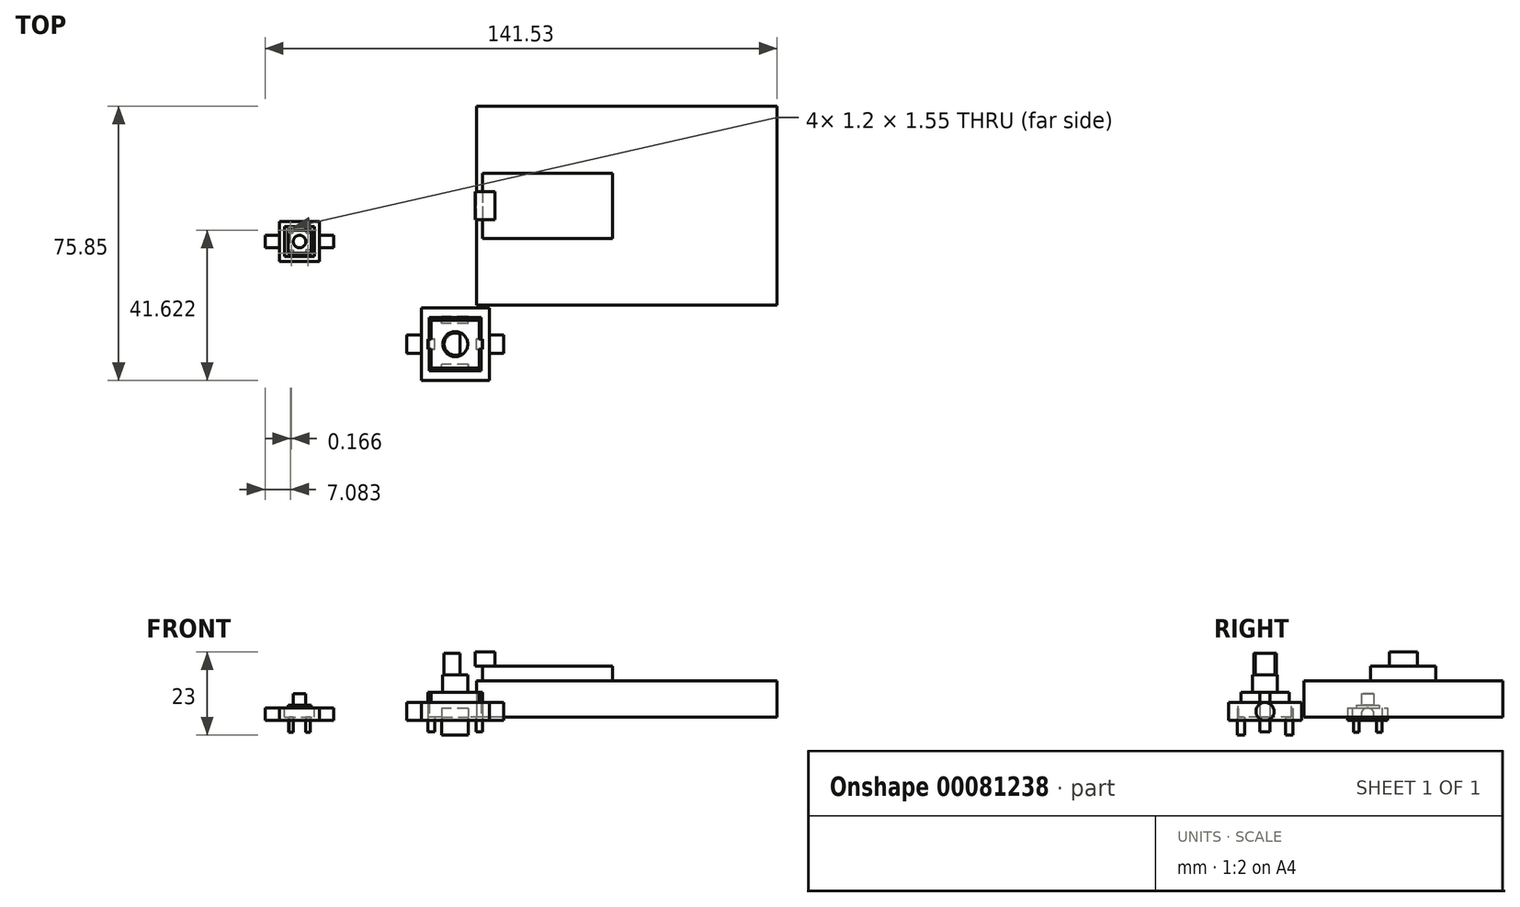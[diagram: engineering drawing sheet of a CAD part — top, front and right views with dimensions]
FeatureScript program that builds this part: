
annotation { "Feature Type Name" : "Feature", "Feature Type Description" : "" }
export const myFeature = defineFeature(function(context is Context, id is Id, definition is map)
    precondition{}
    {
        {
            var Q0;
            Q0=qCreatedBy(makeId("Top.planeOp"),FACE);
            var sketch = newSketch(context, id + "F0", { "sketchPlane" : qUnion([Q0])});
            skLineSegment(sketch, "E0.bottom", {"start": v(-39.86, 25.2) * mm, "end": v(-46.2, 25.2) * mm});
            skLineSegment(sketch, "E0.top", {"start": v(-39.86, 31.54) * mm, "end": v(-46.2, 31.54) * mm});
            skLineSegment(sketch, "E0.left", {"start": v(-39.86, 25.2) * mm, "end": v(-39.86, 31.54) * mm});
            skLineSegment(sketch, "E0.right", {"start": v(-46.2, 25.2) * mm, "end": v(-46.2, 31.54) * mm});
            skPoint(sketch, "E0.middle", {"position": v(-43.03, 28.37) * mm});
            skSolve(sketch);
        }
        {
            var Q0;
            Q0 = qSketchRegion(id + "F0", true);
            extrude(context, id + "F1", {"entities" : qUnion([Q0]), "depth" : 3.3 * mm});
        }
        {
            var Q0;
            Q0=makeQuery(id+"F1.opExtrude","SWEPT_FACE",FACE,{"disambiguationData":[OSD([sQuery(id+"F0.wireOp",EDGE,"E0.bottom")])]});
            var sketch = newSketch(context, id + "F2", { "sketchPlane" : qUnion([Q0])});
            skLineSegment(sketch, "E1.bottom", {"start": v(-40.12, 0.6) * mm, "end": v(-41.32, 0.6) * mm});
            skLineSegment(sketch, "E1.top", {"start": v(-40.12, -4.2) * mm, "end": v(-41.32, -4.2) * mm});
            skLineSegment(sketch, "E1.left", {"start": v(-40.12, 0.6) * mm, "end": v(-40.12, -4.2) * mm});
            skLineSegment(sketch, "E1.right", {"start": v(-41.32, 0.6) * mm, "end": v(-41.32, -4.2) * mm});
            skLineSegment(sketch, "E2", {"start": v(-43.03, 3.3) * mm, "end": v(-43.03, 2.27) * mm, "construction": true});
            skPoint(sketch, "E2.endSnap0", {"position": v(-43.03, 3.3) * mm});
            skLineSegment(sketch, "E3.MirrorCS", {"start": v(-44.74, 0.6) * mm, "end": v(-44.74, -4.2) * mm});
            skLineSegment(sketch, "E4.MirrorCS", {"start": v(-45.94, 0.6) * mm, "end": v(-44.74, 0.6) * mm});
            skLineSegment(sketch, "E5.MirrorCS", {"start": v(-45.94, 0.6) * mm, "end": v(-45.94, -4.2) * mm});
            skLineSegment(sketch, "E6.MirrorCS", {"start": v(-45.94, -4.2) * mm, "end": v(-44.74, -4.2) * mm});
            skSolve(sketch);
        }
        {
            var Q0;
            Q0=makeQuery(id+"F1.opExtrude","SWEPT_FACE",FACE,{"disambiguationData":[OSD([sQuery(id+"F0.wireOp",EDGE,"E0.top")])]});
            var sketch = newSketch(context, id + "F3", { "sketchPlane" : qUnion([Q0])});
            skLineSegment(sketch, "E7.bottom", {"start": v(46.1, 0.58) * mm, "end": v(44.9, 0.58) * mm});
            skLineSegment(sketch, "E7.top", {"start": v(46.1, -4.22) * mm, "end": v(44.9, -4.22) * mm});
            skLineSegment(sketch, "E7.left", {"start": v(46.1, 0.58) * mm, "end": v(46.1, -4.22) * mm});
            skLineSegment(sketch, "E7.right", {"start": v(44.9, 0.58) * mm, "end": v(44.9, -4.22) * mm});
            skLineSegment(sketch, "E8", {"start": v(43.09, 5.78) * mm, "end": v(43.09, 4.76) * mm, "construction": true});
            skPoint(sketch, "E8.endSnap0", {"position": v(43.09, 3.28) * mm});
            skLineSegment(sketch, "E9.MirrorCS", {"start": v(41.27, 0.58) * mm, "end": v(41.27, -4.22) * mm});
            skLineSegment(sketch, "E10.MirrorCS", {"start": v(40.07, 0.58) * mm, "end": v(41.27, 0.58) * mm});
            skLineSegment(sketch, "E11.MirrorCS", {"start": v(40.07, 0.58) * mm, "end": v(40.07, -4.22) * mm});
            skLineSegment(sketch, "E12.MirrorCS", {"start": v(40.07, -4.22) * mm, "end": v(41.27, -4.22) * mm});
            skSolve(sketch);
        }
        {
            var Q0;
            Q0 = qSketchRegion(id + "F3", true);
            var Q1;
            Q1 = qSketchRegion(id + "F2", true);
            extrude(context, id + "F4", {"entities" : qUnion([Q0, Q1]), "operationType" : NewBodyOperationType.ADD, "endBound" : BoundingType.SYMMETRIC, "depth" : 1.55 * mm});
        }
        {
            var Q0;
            Q0=makeQuery(id+"F1.opExtrude","CAP_FACE",FACE,{"disambiguationData":[OSD([sQuery(id+"F0.wireOp",EDGE,"E0.bottom"),sQuery(id+"F0.wireOp",EDGE,"E0.top"),sQuery(id+"F0.wireOp",EDGE,"E0.left"),sQuery(id+"F0.wireOp",EDGE,"E0.right")])],"isStart":false});
            var sketch = newSketch(context, id + "F5", { "sketchPlane" : qUnion([Q0])});
            skCircle(sketch, "E13", {"center": v(-43.03, 28.37) * mm, "radius": 1.73 * mm});
            skPoint(sketch, "E13.centerSnap0", {"position": v(-43.03, 31.54) * mm});
            skPoint(sketch, "E13.centerSnap1", {"position": v(-39.86, 28.37) * mm});
            skSolve(sketch);
        }
        {
            var Q0;
            Q0 = qSketchRegion(id + "F5", true);
            extrude(context, id + "F6", {"entities" : qUnion([Q0]), "operationType" : NewBodyOperationType.ADD, "depth" : 3.19 * mm});
        }
        {
            var Q0;
            Q0=qCreatedBy(makeId("Top.planeOp"),FACE);
            var sketch = newSketch(context, id + "F7", { "sketchPlane" : qUnion([Q0])});
            skLineSegment(sketch, "E14.bottom", {"start": v(-6.65, -6.65) * mm, "end": v(6.65, -6.65) * mm});
            skLineSegment(sketch, "E14.top", {"start": v(-6.65, 6.65) * mm, "end": v(6.65, 6.65) * mm});
            skLineSegment(sketch, "E14.left", {"start": v(-6.65, -6.65) * mm, "end": v(-6.65, 6.65) * mm});
            skLineSegment(sketch, "E14.right", {"start": v(6.65, -6.65) * mm, "end": v(6.65, 6.65) * mm});
            skPoint(sketch, "E14.middle", {"position": v(0, 0) * mm});
            skSolve(sketch);
        }
        {
            var Q0;
            Q0 = qSketchRegion(id + "F7", true);
            extrude(context, id + "F8", {"entities" : qUnion([Q0]), "depth" : 6.8 * mm});
        }
        {
            var Q0;
            Q0=makeQuery(id+"F8.opExtrude","SWEPT_FACE",FACE,{"disambiguationData":[OSD([sQuery(id+"F7.wireOp",EDGE,"E14.left")])]});
            var sketch = newSketch(context, id + "F9", { "sketchPlane" : qUnion([Q0])});
            skLineSegment(sketch, "E15.bottom", {"start": v(-1.36, 6.8) * mm, "end": v(1.44, 6.8) * mm});
            skLineSegment(sketch, "E15.top", {"start": v(-1.36, -4.1) * mm, "end": v(1.44, -4.1) * mm});
            skLineSegment(sketch, "E15.left", {"start": v(-1.36, 6.8) * mm, "end": v(-1.36, -4.1) * mm});
            skLineSegment(sketch, "E15.right", {"start": v(1.44, 6.8) * mm, "end": v(1.44, -4.1) * mm});
            skSolve(sketch);
        }
        {
            var Q0;
            Q0=makeQuery(id+"F8.opExtrude","SWEPT_FACE",FACE,{"disambiguationData":[OSD([sQuery(id+"F7.wireOp",EDGE,"E14.right")])]});
            var sketch = newSketch(context, id + "F10", { "sketchPlane" : qUnion([Q0])});
            skLineSegment(sketch, "E16.bottom", {"start": v(-1.46, 6.8) * mm, "end": v(1.34, 6.8) * mm});
            skLineSegment(sketch, "E16.top", {"start": v(-1.46, -4.1) * mm, "end": v(1.34, -4.1) * mm});
            skLineSegment(sketch, "E16.left", {"start": v(-1.46, 6.8) * mm, "end": v(-1.46, -4.1) * mm});
            skLineSegment(sketch, "E16.right", {"start": v(1.34, 6.8) * mm, "end": v(1.34, -4.1) * mm});
            skSolve(sketch);
        }
        {
            var Q0;
            Q0 = qSketchRegion(id + "F10", true);
            var Q1;
            Q1 = qSketchRegion(id + "F9", true);
            extrude(context, id + "F11", {"entities" : qUnion([Q0, Q1]), "operationType" : NewBodyOperationType.ADD, "endBound" : BoundingType.SYMMETRIC, "depth" : 1.85 * mm});
        }
        {
            var Q0;
            Q0=makeQuery(id+"F8.opExtrude","SWEPT_FACE",FACE,{"disambiguationData":[OSD([sQuery(id+"F7.wireOp",EDGE,"E14.top")])]});
            var sketch = newSketch(context, id + "F12", { "sketchPlane" : qUnion([Q0])});
            skLineSegment(sketch, "E17.bottom", {"start": v(-3.55, 2.3) * mm, "end": v(3.75, 2.3) * mm});
            skLineSegment(sketch, "E17.top", {"start": v(-3.55, -5) * mm, "end": v(3.75, -5) * mm});
            skLineSegment(sketch, "E17.left", {"start": v(-3.55, 2.3) * mm, "end": v(-3.55, -5) * mm});
            skLineSegment(sketch, "E17.right", {"start": v(3.75, 2.3) * mm, "end": v(3.75, -5) * mm});
            skSolve(sketch);
        }
        {
            var Q0;
            Q0=makeQuery(id+"F8.opExtrude","SWEPT_FACE",FACE,{"disambiguationData":[OSD([sQuery(id+"F7.wireOp",EDGE,"E14.bottom")])]});
            var sketch = newSketch(context, id + "F13", { "sketchPlane" : qUnion([Q0])});
            skLineSegment(sketch, "E18.0", {"start": v(3.55, 2.3) * mm, "end": v(-3.75, 2.3) * mm});
            skLineSegment(sketch, "E19.0", {"start": v(-3.75, 2.3) * mm, "end": v(-3.75, -5) * mm});
            skLineSegment(sketch, "E20.0", {"start": v(3.55, -5) * mm, "end": v(-3.75, -5) * mm});
            skLineSegment(sketch, "E21.0", {"start": v(3.55, 2.3) * mm, "end": v(3.55, -5) * mm});
            skSolve(sketch);
        }
        {
            var Q0;
            Q0 = qSketchRegion(id + "F13", true);
            var Q1;
            Q1 = qSketchRegion(id + "F12", true);
            extrude(context, id + "F14", {"entities" : qUnion([Q0, Q1]), "operationType" : NewBodyOperationType.ADD, "endBound" : BoundingType.SYMMETRIC, "depth" : 2 * mm});
        }
        {
            var Q0;
            Q0=makeQuery(id+"F11.boolean.opBoolean","MERGE",FACE,{"derivedFrom":[makeQuery(id+"F8.opExtrude","CAP_FACE",FACE,{"disambiguationData":[OSD([sQuery(id+"F7.wireOp",EDGE,"E14.bottom"),sQuery(id+"F7.wireOp",EDGE,"E14.top"),sQuery(id+"F7.wireOp",EDGE,"E14.left"),sQuery(id+"F7.wireOp",EDGE,"E14.right")])],"isStart":false}),makeQuery(id+"F11.opExtrude","SWEPT_FACE",FACE,{"disambiguationData":[OSD([sQuery(id+"F9.wireOp",EDGE,"E15.bottom")])]}),makeQuery(id+"F11.opExtrude","SWEPT_FACE",FACE,{"disambiguationData":[OSD([sQuery(id+"F10.wireOp",EDGE,"E16.bottom")])]})]});
            var sketch = newSketch(context, id + "F15", { "sketchPlane" : qUnion([Q0])});
            skCircle(sketch, "E22", {"center": v(0, 0) * mm, "radius": 3.45 * mm});
            skSolve(sketch);
        }
        {
            var Q0;
            Q0 = qSketchRegion(id + "F15", true);
            extrude(context, id + "F16", {"entities" : qUnion([Q0]), "operationType" : NewBodyOperationType.ADD, "depth" : 4.8 * mm});
        }
        {
            var Q0;
            Q0=makeQuery(id+"F16.opExtrude","CAP_FACE",FACE,{"disambiguationData":[OSD([sQuery(id+"F15.wireOp",EDGE,"E22")])],"isStart":false});
            var sketch = newSketch(context, id + "F17", { "sketchPlane" : qUnion([Q0])});
            skCircle(sketch, "E23", {"center": v(0, 0) * mm, "radius": 3.08 * mm});
            skSolve(sketch);
        }
        {
            var Q0;
            Q0 = qSketchRegion(id + "F17", true);
            extrude(context, id + "F18", {"entities" : qUnion([Q0]), "operationType" : NewBodyOperationType.ADD, "depth" : 6 * mm});
        }
        {
            var Q0;
            Q0=makeQuery(id+"F18.opExtrude","CAP_FACE",FACE,{"disambiguationData":[OSD([sQuery(id+"F17.wireOp",EDGE,"E23")])],"isStart":false});
            var sketch = newSketch(context, id + "F19", { "sketchPlane" : qUnion([Q0])});
            skArc(sketch, "E24.0", {"start": v(1.38, -2.75) * mm, "mid": v(3.08, 0) * mm, "end": v(1.38, 2.75) * mm});
            skLineSegment(sketch, "E25", {"start": v(1.38, 2.75) * mm, "end": v(1.38, -2.75) * mm});
            skLineSegment(sketch, "E26", {"start": v(1.82, 0) * mm, "end": v(3.08, 0) * mm, "construction": true});
            skSolve(sketch);
        }
        {
            var Q0;
            Q0 = qSketchRegion(id + "F19", true);
            var Q1;
            Q1=makeQuery(id+"F16.opExtrude","CAP_FACE",FACE,{"disambiguationData":[OSD([sQuery(id+"F15.wireOp",EDGE,"E22")])],"isStart":false});
            extrude(context, id + "F20", {"entities" : qUnion([Q0]), "operationType" : NewBodyOperationType.REMOVE, "endBound" : BoundingType.UP_TO_SURFACE, "oppositeDirection" : true, "endBoundEntityFace" : qUnion([Q1]), "depth" : 25 * mm});
        }
        {
            var Q0;
            Q0=qCreatedBy(makeId("Top.planeOp"),FACE);
            var sketch = newSketch(context, id + "F21", { "sketchPlane" : qUnion([Q0])});
            skLineSegment(sketch, "E27.bottom", {"start": v(88.94, 10.77) * mm, "end": v(5.94, 10.77) * mm});
            skLineSegment(sketch, "E27.top", {"start": v(88.94, 65.77) * mm, "end": v(5.94, 65.77) * mm});
            skLineSegment(sketch, "E27.left", {"start": v(88.94, 10.77) * mm, "end": v(88.94, 65.77) * mm});
            skLineSegment(sketch, "E27.right", {"start": v(5.94, 10.77) * mm, "end": v(5.94, 65.77) * mm});
            skPoint(sketch, "E27.middle", {"position": v(47.44, 38.27) * mm});
            skSolve(sketch);
        }
        {
            var Q0;
            Q0 = qSketchRegion(id + "F21", true);
            extrude(context, id + "F22", {"entities" : qUnion([Q0]), "depth" : 10 * mm});
        }
        {
            var Q0;
            Q0=makeQuery(id+"F22.opExtrude","CAP_FACE",FACE,{"disambiguationData":[OSD([sQuery(id+"F21.wireOp",EDGE,"E27.bottom"),sQuery(id+"F21.wireOp",EDGE,"E27.top"),sQuery(id+"F21.wireOp",EDGE,"E27.left"),sQuery(id+"F21.wireOp",EDGE,"E27.right")])],"isStart":false});
            var sketch = newSketch(context, id + "F23", { "sketchPlane" : qUnion([Q0])});
            skLineSegment(sketch, "E28.bottom", {"start": v(7.53, 47.27) * mm, "end": v(43.53, 47.27) * mm});
            skLineSegment(sketch, "E28.top", {"start": v(7.53, 29.17) * mm, "end": v(43.53, 29.17) * mm});
            skLineSegment(sketch, "E28.left", {"start": v(7.53, 47.27) * mm, "end": v(7.53, 29.17) * mm});
            skLineSegment(sketch, "E28.right", {"start": v(43.53, 47.27) * mm, "end": v(43.53, 29.17) * mm});
            skSolve(sketch);
        }
        {
            var Q0;
            Q0 = qSketchRegion(id + "F23", true);
            extrude(context, id + "F24", {"entities" : qUnion([Q0]), "operationType" : NewBodyOperationType.ADD, "depth" : 4 * mm});
        }
        {
            var Q0;
            Q0=makeQuery(id+"F24.opExtrude","CAP_FACE",FACE,{"disambiguationData":[OSD([sQuery(id+"F23.wireOp",EDGE,"E28.bottom"),sQuery(id+"F23.wireOp",EDGE,"E28.top"),sQuery(id+"F23.wireOp",EDGE,"E28.left"),sQuery(id+"F23.wireOp",EDGE,"E28.right")])],"isStart":false});
            var sketch = newSketch(context, id + "F25", { "sketchPlane" : qUnion([Q0])});
            skLineSegment(sketch, "E29.bottom", {"start": v(11.03, 42.12) * mm, "end": v(5.53, 42.12) * mm});
            skLineSegment(sketch, "E29.top", {"start": v(11.03, 34.42) * mm, "end": v(5.53, 34.42) * mm});
            skLineSegment(sketch, "E29.left", {"start": v(11.03, 42.12) * mm, "end": v(11.03, 34.42) * mm});
            skLineSegment(sketch, "E29.right", {"start": v(5.53, 42.12) * mm, "end": v(5.53, 34.42) * mm});
            skSolve(sketch);
        }
        {
            var Q0;
            Q0 = qSketchRegion(id + "F25", true);
            extrude(context, id + "F26", {"entities" : qUnion([Q0]), "operationType" : NewBodyOperationType.ADD, "depth" : 4 * mm});
        }
        {
            var Q0;
            Q0=makeQuery(id+"F1.opExtrude","CAP_FACE",FACE,{"disambiguationData":[OSD([sQuery(id+"F0.wireOp",EDGE,"E0.bottom"),sQuery(id+"F0.wireOp",EDGE,"E0.top"),sQuery(id+"F0.wireOp",EDGE,"E0.left"),sQuery(id+"F0.wireOp",EDGE,"E0.right")])],"isStart":true});
            var sketch = newSketch(context, id + "F27", { "sketchPlane" : qUnion([Q0])});
            skLineSegment(sketch, "E30.bottom", {"start": v(-37.59, -22.87) * mm, "end": v(-48.59, -22.87) * mm});
            skLineSegment(sketch, "E30.top", {"start": v(-37.59, -33.87) * mm, "end": v(-48.59, -33.87) * mm});
            skLineSegment(sketch, "E30.left", {"start": v(-37.59, -22.87) * mm, "end": v(-37.59, -33.87) * mm});
            skLineSegment(sketch, "E30.right", {"start": v(-48.59, -22.87) * mm, "end": v(-48.59, -33.87) * mm});
            skPoint(sketch, "E30.middle", {"position": v(-43.09, -28.37) * mm});
            skPoint(sketch, "E30.middle.positionSnap0", {"position": v(-43.09, -31.54) * mm});
            skPoint(sketch, "E30.middle.positionSnap1", {"position": v(-46.2, -28.37) * mm});
            skPoint(sketch, "E30.centerSnap0", {"position": v(-43.09, -31.54) * mm});
            skPoint(sketch, "E30.centerSnap1", {"position": v(-46.2, -28.37) * mm});
            skSolve(sketch);
        }
        {
            var Q0;
            Q0 = qSketchRegion(id + "F27", true);
            extrude(context, id + "F28", {"entities" : qUnion([Q0]), "oppositeDirection" : true, "depth" : 2.5 * mm, "hasSecondDirection" : true, "secondDirectionOppositeDirection" : false, "secondDirectionDepth" : 1 * mm});
        }
        {
            var Q0;
            Q0=makeQuery(id+"F1.opExtrude","SWEPT_BODY",BODY,{"disambiguationData":[OSD([sQuery(id+"F0.wireOp",EDGE,"E0.bottom"),sQuery(id+"F0.wireOp",EDGE,"E0.top"),sQuery(id+"F0.wireOp",EDGE,"E0.left"),sQuery(id+"F0.wireOp",EDGE,"E0.right")])]});
            var Q1;
            Q1=makeQuery(id+"F28.opExtrude","SWEPT_BODY",BODY,{"disambiguationData":[OSD([sQuery(id+"F27.wireOp",EDGE,"E30.bottom"),sQuery(id+"F27.wireOp",EDGE,"E30.top"),sQuery(id+"F27.wireOp",EDGE,"E30.left"),sQuery(id+"F27.wireOp",EDGE,"E30.right")])]});
            booleanBodies(context, id + "F29", {"operationType" : BooleanOperationType.SUBTRACTION, "tools" : qUnion([Q0]), "targets" : qUnion([Q1]), "keepTools" : true});
        }
        {
            var Q0;
            Q0=makeQuery(id+"F28.opExtrude","CAP_FACE",FACE,{"disambiguationData":[OSD([sQuery(id+"F27.wireOp",EDGE,"E30.bottom"),sQuery(id+"F27.wireOp",EDGE,"E30.top"),sQuery(id+"F27.wireOp",EDGE,"E30.left"),sQuery(id+"F27.wireOp",EDGE,"E30.right")])],"isStart":false});
            var sketch = newSketch(context, id + "F30", { "sketchPlane" : qUnion([Q0])});
            skLineSegment(sketch, "E31.0", {"start": v(-39.86, 25.2) * mm, "end": v(-39.86, 31.54) * mm, "construction": true});
            skLineSegment(sketch, "E32.0", {"start": v(-39.86, 31.54) * mm, "end": v(-46.2, 31.54) * mm, "construction": true});
            skLineSegment(sketch, "E33.0", {"start": v(-46.2, 25.2) * mm, "end": v(-46.2, 31.54) * mm, "construction": true});
            skLineSegment(sketch, "E34.0", {"start": v(-39.86, 25.2) * mm, "end": v(-46.2, 25.2) * mm, "construction": true});
            skLineSegment(sketch, "E35.0", {"start": v(-38.9, 24.24) * mm, "end": v(-38.9, 32.5) * mm});
            skLineSegment(sketch, "E35.1", {"start": v(-38.9, 24.24) * mm, "end": v(-47.16, 24.24) * mm});
            skLineSegment(sketch, "E35.2", {"start": v(-47.16, 24.24) * mm, "end": v(-47.16, 32.5) * mm});
            skLineSegment(sketch, "E35.3", {"start": v(-38.9, 32.5) * mm, "end": v(-47.16, 32.5) * mm});
            skSolve(sketch);
        }
        {
            var Q0;
            Q0 = qSketchRegion(id + "F30", true);
            var Q1;
            Q1=makeQuery(id+"F29.opBoolean","COPY",FACE,{"derivedFrom":makeQuery(id+"F1.opExtrude","CAP_FACE",FACE,{"disambiguationData":[OSD([sQuery(id+"F0.wireOp",EDGE,"E0.bottom"),sQuery(id+"F0.wireOp",EDGE,"E0.top"),sQuery(id+"F0.wireOp",EDGE,"E0.left"),sQuery(id+"F0.wireOp",EDGE,"E0.right")])],"isStart":true})});
            extrude(context, id + "F31", {"entities" : qUnion([Q0]), "operationType" : NewBodyOperationType.REMOVE, "endBound" : BoundingType.UP_TO_SURFACE, "oppositeDirection" : true, "endBoundEntityFace" : qUnion([Q1]), "depth" : 25 * mm});
        }
        {
            var Q0;
            Q0=makeQuery(id+"F28.opExtrude","SWEPT_FACE",FACE,{"disambiguationData":[OSD([sQuery(id+"F27.wireOp",EDGE,"E30.right")])]});
            var sketch = newSketch(context, id + "F32", { "sketchPlane" : qUnion([Q0])});
            skCircle(sketch, "E36", {"center": v(-28.37, 0.75) * mm, "radius": 1.75 * mm});
            skPoint(sketch, "E36.centerSnap0", {"position": v(-28.37, -1) * mm});
            skPoint(sketch, "E36.centerSnap1", {"position": v(-22.87, 0.75) * mm});
            skSolve(sketch);
        }
        {
            var Q0;
            Q0 = qSketchRegion(id + "F32", true);
            extrude(context, id + "F33", {"entities" : qUnion([Q0]), "operationType" : NewBodyOperationType.ADD, "depth" : 4 * mm});
        }
        {
            var Q0;
            Q0=makeQuery(id+"F28.opExtrude","SWEPT_FACE",FACE,{"disambiguationData":[OSD([sQuery(id+"F27.wireOp",EDGE,"E30.left")])]});
            var sketch = newSketch(context, id + "F34", { "sketchPlane" : qUnion([Q0])});
            skCircle(sketch, "E37", {"center": v(28.37, 0.75) * mm, "radius": 1.75 * mm});
            skPoint(sketch, "E37.centerSnap0", {"position": v(28.37, -0.98) * mm});
            skPoint(sketch, "E37.centerSnap1", {"position": v(33.91, 0.75) * mm});
            skPoint(sketch, "E38", {"position": v(28.37, -1) * mm});
            skPoint(sketch, "E39", {"position": v(33.87, 0.75) * mm});
            skSolve(sketch);
        }
        {
            var Q0;
            Q0 = qSketchRegion(id + "F34", true);
            extrude(context, id + "F35", {"entities" : qUnion([Q0]), "operationType" : NewBodyOperationType.ADD, "depth" : 4 * mm});
        }
        {
            var Q0;
            Q0=makeQuery(id+"F8.opExtrude","CAP_FACE",FACE,{"disambiguationData":[OSD([sQuery(id+"F7.wireOp",EDGE,"E14.bottom"),sQuery(id+"F7.wireOp",EDGE,"E14.top"),sQuery(id+"F7.wireOp",EDGE,"E14.left"),sQuery(id+"F7.wireOp",EDGE,"E14.right")])],"isStart":true});
            var sketch = newSketch(context, id + "F36", { "sketchPlane" : qUnion([Q0])});
            skLineSegment(sketch, "E40.bottom", {"start": v(-9.41, -10.08) * mm, "end": v(9.41, -10.08) * mm});
            skLineSegment(sketch, "E40.top", {"start": v(-9.41, 10.08) * mm, "end": v(9.41, 10.08) * mm});
            skLineSegment(sketch, "E40.left", {"start": v(-9.41, -10.08) * mm, "end": v(-9.41, 10.08) * mm});
            skLineSegment(sketch, "E40.right", {"start": v(9.41, -10.08) * mm, "end": v(9.41, 10.08) * mm});
            skPoint(sketch, "E40.middle", {"position": v(0, 0) * mm});
            skSolve(sketch);
        }
        {
            var Q0;
            Q0 = qSketchRegion(id + "F36", true);
            extrude(context, id + "F37", {"entities" : qUnion([Q0]), "oppositeDirection" : true, "depth" : 4 * mm, "hasSecondDirection" : true, "secondDirectionOppositeDirection" : false, "secondDirectionDepth" : 1 * mm});
        }
        {
            var Q0;
            Q0=makeQuery(id+"F8.opExtrude","SWEPT_BODY",BODY,{"disambiguationData":[OSD([sQuery(id+"F7.wireOp",EDGE,"E14.bottom"),sQuery(id+"F7.wireOp",EDGE,"E14.top"),sQuery(id+"F7.wireOp",EDGE,"E14.left"),sQuery(id+"F7.wireOp",EDGE,"E14.right")])]});
            var Q1;
            Q1=makeQuery(id+"F37.opExtrude","SWEPT_BODY",BODY,{"disambiguationData":[OSD([sQuery(id+"F36.wireOp",EDGE,"E40.bottom"),sQuery(id+"F36.wireOp",EDGE,"E40.top"),sQuery(id+"F36.wireOp",EDGE,"E40.left"),sQuery(id+"F36.wireOp",EDGE,"E40.right")])]});
            var Q2;
            Q2=makeQuery(id+"F8.opExtrude","SWEPT_FACE",FACE,{"disambiguationData":[OSD([sQuery(id+"F7.wireOp",EDGE,"E14.bottom")])]});
            var Q3;
            {var subQ0=sQuery(id+"F7.wireOp",EDGE,"E14.right");var subQ3=sQuery(id+"F7.wireOp",EDGE,"E14.bottom");Q3=makeQuery(id+"F11.boolean.opBoolean","SPLIT",FACE,{"disambiguationData":[TD([makeQuery(id+"F8.opExtrude","SWEPT_FACE",FACE,{"disambiguationData":[OSD([subQ3])]})])],"derivedFrom":makeQuery(id+"F8.opExtrude","SWEPT_FACE",FACE,{"disambiguationData":[OSD([subQ0])]})});}
            var Q4;
            Q4=makeQuery(id+"F11.opExtrude","CAP_FACE",FACE,{"disambiguationData":[OSD([sQuery(id+"F10.wireOp",EDGE,"E16.bottom"),sQuery(id+"F10.wireOp",EDGE,"E16.top"),sQuery(id+"F10.wireOp",EDGE,"E16.left"),sQuery(id+"F10.wireOp",EDGE,"E16.right")])],"isStart":false});
            var Q5;
            {var subQ0=sQuery(id+"F7.wireOp",EDGE,"E14.right");var subQ2=sQuery(id+"F7.wireOp",EDGE,"E14.top");Q5=makeQuery(id+"F11.boolean.opBoolean","SPLIT",FACE,{"disambiguationData":[TD([makeQuery(id+"F8.opExtrude","SWEPT_FACE",FACE,{"disambiguationData":[OSD([subQ2])]})])],"derivedFrom":makeQuery(id+"F8.opExtrude","SWEPT_FACE",FACE,{"disambiguationData":[OSD([subQ0])]})});}
            var Q6;
            Q6=makeQuery(id+"F8.opExtrude","SWEPT_FACE",FACE,{"disambiguationData":[OSD([sQuery(id+"F7.wireOp",EDGE,"E14.top")])]});
            var Q7;
            {var subQ1=sQuery(id+"F7.wireOp",EDGE,"E14.left");var subQ2=sQuery(id+"F7.wireOp",EDGE,"E14.top");Q7=makeQuery(id+"F11.boolean.opBoolean","SPLIT",FACE,{"disambiguationData":[TD([makeQuery(id+"F8.opExtrude","SWEPT_FACE",FACE,{"disambiguationData":[OSD([subQ2])]})])],"derivedFrom":makeQuery(id+"F8.opExtrude","SWEPT_FACE",FACE,{"disambiguationData":[OSD([subQ1])]})});}
            var Q8;
            Q8=makeQuery(id+"F11.opExtrude","CAP_FACE",FACE,{"disambiguationData":[OSD([sQuery(id+"F9.wireOp",EDGE,"E15.bottom"),sQuery(id+"F9.wireOp",EDGE,"E15.top"),sQuery(id+"F9.wireOp",EDGE,"E15.left"),sQuery(id+"F9.wireOp",EDGE,"E15.right")])],"isStart":true});
            var Q9;
            {var subQ1=sQuery(id+"F7.wireOp",EDGE,"E14.left");var subQ3=sQuery(id+"F7.wireOp",EDGE,"E14.bottom");Q9=makeQuery(id+"F11.boolean.opBoolean","SPLIT",FACE,{"disambiguationData":[TD([makeQuery(id+"F8.opExtrude","SWEPT_FACE",FACE,{"disambiguationData":[OSD([subQ3])]})])],"derivedFrom":makeQuery(id+"F8.opExtrude","SWEPT_FACE",FACE,{"disambiguationData":[OSD([subQ1])]})});}
            booleanBodies(context, id + "F38", {"operationType" : BooleanOperationType.SUBTRACTION, "tools" : qUnion([Q0]), "targets" : qUnion([Q1]), "entitiesToOffset" : qUnion([Q2, Q3, Q4, Q5, Q6, Q7, Q8, Q9]), "keepTools" : true});
        }
        {
            var Q0;
            Q0=makeQuery(id+"F37.opExtrude","CAP_FACE",FACE,{"disambiguationData":[OSD([sQuery(id+"F36.wireOp",EDGE,"E40.bottom"),sQuery(id+"F36.wireOp",EDGE,"E40.top"),sQuery(id+"F36.wireOp",EDGE,"E40.left"),sQuery(id+"F36.wireOp",EDGE,"E40.right")])],"isStart":false});
            var sketch = newSketch(context, id + "F39", { "sketchPlane" : qUnion([Q0])});
            skLineSegment(sketch, "E41.bottom", {"start": v(-7.19, -7.36) * mm, "end": v(7.19, -7.36) * mm});
            skLineSegment(sketch, "E41.top", {"start": v(-7.19, 7.36) * mm, "end": v(7.19, 7.36) * mm});
            skLineSegment(sketch, "E41.left", {"start": v(-7.19, -7.36) * mm, "end": v(-7.19, 7.36) * mm});
            skLineSegment(sketch, "E41.right", {"start": v(7.19, -7.36) * mm, "end": v(7.19, 7.36) * mm});
            skPoint(sketch, "E41.middle", {"position": v(0, 0) * mm});
            skSolve(sketch);
        }
        {
            var Q0;
            Q0 = qSketchRegion(id + "F39", true);
            var Q1;
            Q1=makeQuery(id+"F38.opBoolean","COPY",FACE,{"derivedFrom":makeQuery(id+"F8.opExtrude","CAP_FACE",FACE,{"disambiguationData":[OSD([sQuery(id+"F7.wireOp",EDGE,"E14.bottom"),sQuery(id+"F7.wireOp",EDGE,"E14.top"),sQuery(id+"F7.wireOp",EDGE,"E14.left"),sQuery(id+"F7.wireOp",EDGE,"E14.right")])],"isStart":true})});
            extrude(context, id + "F40", {"entities" : qUnion([Q0]), "operationType" : NewBodyOperationType.REMOVE, "endBound" : BoundingType.UP_TO_SURFACE, "oppositeDirection" : true, "endBoundEntityFace" : qUnion([Q1]), "depth" : 25 * mm});
        }
        {
            var Q0;
            Q0=makeQuery(id+"F37.opExtrude","SWEPT_FACE",FACE,{"disambiguationData":[OSD([sQuery(id+"F36.wireOp",EDGE,"E40.left")])]});
            var sketch = newSketch(context, id + "F41", { "sketchPlane" : qUnion([Q0])});
            skCircle(sketch, "E42", {"center": v(0, 1.5) * mm, "radius": 2.5 * mm});
            skPoint(sketch, "E42.centerSnap0", {"position": v(-10.08, 1.5) * mm});
            skSolve(sketch);
        }
        {
            var Q0;
            Q0 = qSketchRegion(id + "F41", true);
            extrude(context, id + "F42", {"entities" : qUnion([Q0]), "operationType" : NewBodyOperationType.ADD, "depth" : 4 * mm});
        }
        {
            var Q0;
            Q0=makeQuery(id+"F37.opExtrude","SWEPT_FACE",FACE,{"disambiguationData":[OSD([sQuery(id+"F36.wireOp",EDGE,"E40.right")])]});
            var sketch = newSketch(context, id + "F43", { "sketchPlane" : qUnion([Q0])});
            skCircle(sketch, "E43", {"center": v(0, 1.5) * mm, "radius": 2.5 * mm});
            skPoint(sketch, "E43.centerSnap0", {"position": v(-10.08, 1.5) * mm});
            skPoint(sketch, "E43.centerSnap1", {"position": v(0, 4) * mm});
            skSolve(sketch);
        }
        {
            var Q0;
            Q0 = qSketchRegion(id + "F43", true);
            extrude(context, id + "F44", {"entities" : qUnion([Q0]), "operationType" : NewBodyOperationType.ADD, "depth" : 4 * mm});
        }
    });
